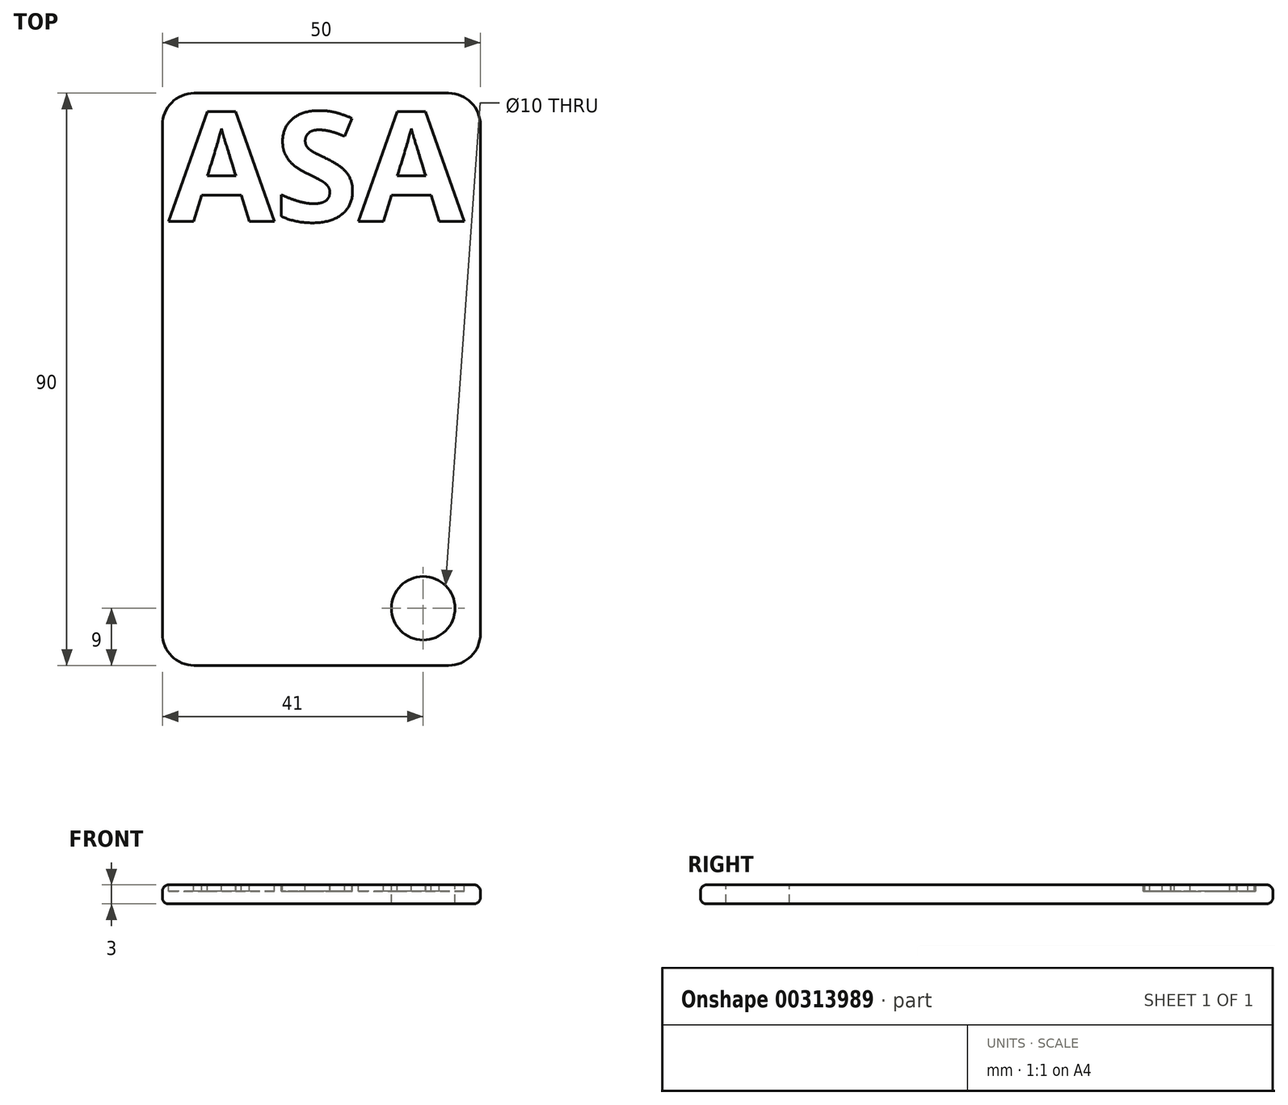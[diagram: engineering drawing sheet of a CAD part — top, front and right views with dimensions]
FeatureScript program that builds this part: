
annotation { "Feature Type Name" : "Feature", "Feature Type Description" : "" }
export const myFeature = defineFeature(function(context is Context, id is Id, definition is map)
    precondition{}
    {
        {
            var Q0;
            Q0=qCreatedBy(makeId("Top.planeOp"),FACE);
            var sketch = newSketch(context, id + "F0", { "sketchPlane" : qUnion([Q0])});
            skLineSegment(sketch, "E0.bottom", {"start": v(-45, 25) * mm, "end": v(45, 25) * mm});
            skLineSegment(sketch, "E0.top", {"start": v(-45, -25) * mm, "end": v(45, -25) * mm});
            skLineSegment(sketch, "E0.left", {"start": v(-45, 25) * mm, "end": v(-45, -25) * mm});
            skLineSegment(sketch, "E0.right", {"start": v(45, 25) * mm, "end": v(45, -25) * mm});
            skLineSegment(sketch, "E1", {"start": v(-45, 25) * mm, "end": v(45, -25) * mm, "construction": true});
            skSolve(sketch);
        }
        {
            var Q0;
            Q0=makeQuery(id+"F0.imprint","IMPRINT",FACE,{"disambiguationData":[TD([[makeQuery(id+"F0.imprint","IMPRINT",EDGE,{"derivedFrom":sQuery(id+"F0.wireOp",EDGE,"E0.bottom")}),-1.0]])]});
            extrude(context, id + "F1", {"entities" : qUnion([Q0]), "depth" : 3 * mm});
        }
        {
            var Q0;
            Q0=makeQuery(id+"F1.opExtrude","CAP_FACE",FACE,{"disambiguationData":[OSD([sQuery(id+"F0.wireOp",EDGE,"E0.bottom"),sQuery(id+"F0.wireOp",EDGE,"E0.top"),sQuery(id+"F0.wireOp",EDGE,"E0.left"),sQuery(id+"F0.wireOp",EDGE,"E0.right")])],"isStart":false});
            var Q1;
            Q1=makeQuery(id+"F1.opExtrude","CAP_FACE",FACE,{"disambiguationData":[OSD([sQuery(id+"F0.wireOp",EDGE,"E0.bottom"),sQuery(id+"F0.wireOp",EDGE,"E0.top"),sQuery(id+"F0.wireOp",EDGE,"E0.left"),sQuery(id+"F0.wireOp",EDGE,"E0.right")])],"isStart":true});
            fillet(context, id + "F2", {"entities" : qUnion([Q0, Q1]), "radius" : 1 * mm, "tangentPropagation" : true, "allowEdgeOverflow" : false});
        }
        {
            var Q0;
            Q0=makeQuery(id+"F1.opExtrude","SWEPT_EDGE",EDGE,{"disambiguationData":[OSD([sQuery(id+"F0.wireOp",EDGE,"E0.top"),sQuery(id+"F0.wireOp",EDGE,"E0.right")])]});
            var Q1;
            Q1=makeQuery(id+"F1.opExtrude","SWEPT_EDGE",EDGE,{"disambiguationData":[OSD([sQuery(id+"F0.wireOp",EDGE,"E0.bottom"),sQuery(id+"F0.wireOp",EDGE,"E0.right")])]});
            var Q2;
            Q2=makeQuery(id+"F1.opExtrude","SWEPT_EDGE",EDGE,{"disambiguationData":[OSD([sQuery(id+"F0.wireOp",EDGE,"E0.bottom"),sQuery(id+"F0.wireOp",EDGE,"E0.left")])]});
            var Q3;
            Q3=makeQuery(id+"F1.opExtrude","SWEPT_EDGE",EDGE,{"disambiguationData":[OSD([sQuery(id+"F0.wireOp",EDGE,"E0.top"),sQuery(id+"F0.wireOp",EDGE,"E0.left")])]});
            fillet(context, id + "F3", {"entities" : qUnion([Q0, Q1, Q2, Q3]), "radius" : 5 * mm, "tangentPropagation" : true, "allowEdgeOverflow" : false});
        }
        {
            var Q0;
            Q0=qCreatedBy(makeId("Right.planeOp"),FACE);
            var sketch = newSketch(context, id + "F4", { "sketchPlane" : qUnion([Q0])});
            skLineSegment(sketch, "E2", {"start": v(0, 0) * mm, "end": v(0, 32.9) * mm});
            skSolve(sketch);
        }
        {
            var Q0;
            Q0=makeQuery(id+"F1.opExtrude","SWEPT_BODY",BODY,{"disambiguationData":[OSD([sQuery(id+"F0.wireOp",EDGE,"E0.bottom"),sQuery(id+"F0.wireOp",EDGE,"E0.top"),sQuery(id+"F0.wireOp",EDGE,"E0.left"),sQuery(id+"F0.wireOp",EDGE,"E0.right")])]});
            var Q1;
            Q1=sQuery(id+"F4.wireOp",EDGE,"E2");
            transform(context, id + "F5", {"entities" : qUnion([Q0]), "transformType" : TransformType.ROTATION, "transformAxis" : qUnion([Q1]), "angle" : 90 * degree, "makeCopy" : false});
        }
        {
            var Q0;
            Q0=makeQuery(id+"F1.opExtrude","CAP_FACE",FACE,{"disambiguationData":[OSD([sQuery(id+"F0.wireOp",EDGE,"E0.bottom"),sQuery(id+"F0.wireOp",EDGE,"E0.top"),sQuery(id+"F0.wireOp",EDGE,"E0.left"),sQuery(id+"F0.wireOp",EDGE,"E0.right")])],"isStart":false});
            var sketch = newSketch(context, id + "F6", { "sketchPlane" : qUnion([Q0])});
            skText(sketch, "E3", { "text": "ASA\n", "fontName": "OpenSans-Bold.ttf"});
            const initialGuessF6  = {"E3": [-0.024, 0.02485, 1, 0, 0.01732]};
            skSetInitialGuess(sketch, initialGuessF6);
            skSolve(sketch);
        }
        {
            var Q0;
            Q0=qSketchRegion(id+"F6",true);
            extrude(context, id + "F7", {"entities" : qUnion([Q0]), "operationType" : NewBodyOperationType.REMOVE, "oppositeDirection" : true, "depth" : 1 * mm});
        }
        {
            var Q0;
            {var subQ0=sQuery(id+"F0.wireOp",EDGE,"E0.left");var subQ2=sQuery(id+"F0.wireOp",EDGE,"E0.bottom");var subQ4=sQuery(id+"F0.wireOp",EDGE,"E0.right");var subQ6=sQuery(id+"F0.wireOp",EDGE,"E0.top");Q0=makeQuery(id+"F7.boolean.opBoolean","SPLIT",FACE,{"disambiguationData":[TD([makeQuery(id+"F7.opExtrude","SWEPT_FACE",FACE,{"disambiguationData":[OSD([sQuery(id+"F6.wireOp",EDGE,"E3.sketch_text.stroke-0")])]})])],"derivedFrom":makeQuery(id+"F1.opExtrude","CAP_FACE",FACE,{"disambiguationData":[OSD([subQ2,subQ6,subQ0,subQ4])],"isStart":false})});}
            var sketch = newSketch(context, id + "F8", { "sketchPlane" : qUnion([Q0])});
            skCircle(sketch, "E4", {"center": v(16, -36) * mm, "radius": 5 * mm});
            skSolve(sketch);
        }
        {
            var Q0;
            Q0=qSketchRegion(id+"F8",true);
            extrude(context, id + "F9", {"entities" : qUnion([Q0]), "operationType" : NewBodyOperationType.REMOVE, "oppositeDirection" : true, "depth" : 3 * mm});
        }
    });
